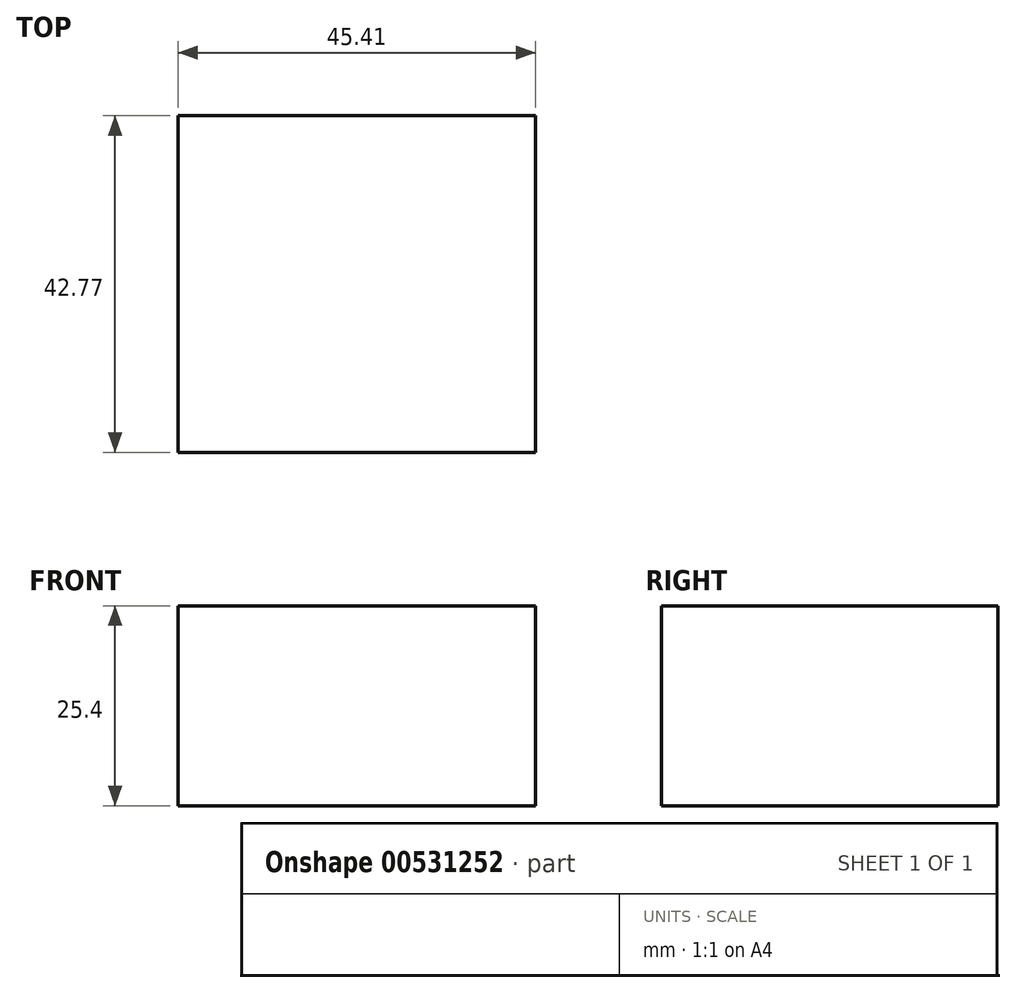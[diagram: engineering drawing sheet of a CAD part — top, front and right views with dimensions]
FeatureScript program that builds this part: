
annotation { "Feature Type Name" : "Feature", "Feature Type Description" : "" }
export const myFeature = defineFeature(function(context is Context, id is Id, definition is map)
    precondition{}
    {
        {
            var Q0;
            Q0=qCreatedBy(makeId("Top.planeOp"),FACE);
            var sketch = newSketch(context, id + "F0", { "sketchPlane" : qUnion([Q0])});
            skLineSegment(sketch, "E0.bottom", {"start": v(0, 0) * mm, "end": v(45.4, 0) * mm});
            skLineSegment(sketch, "E0.top", {"start": v(0, 42.77) * mm, "end": v(45.4, 42.77) * mm});
            skLineSegment(sketch, "E0.left", {"start": v(0, 0) * mm, "end": v(0, 42.77) * mm});
            skLineSegment(sketch, "E0.right", {"start": v(45.4, 0) * mm, "end": v(45.4, 42.77) * mm});
            skSolve(sketch);
        }
        {
            var Q0;
            Q0=makeQuery(id+"F0.imprint","IMPRINT",FACE,{"disambiguationData":[TD([[makeQuery(id+"F0.imprint","IMPRINT",EDGE,{"derivedFrom":sQuery(id+"F0.wireOp",EDGE,"E0.bottom")}),1.0]])]});
            extrude(context, id + "F1", {"entities" : qUnion([Q0]), "depth" : 25.4 * mm, "offsetDistance" : 25.4 * mm});
        }
    });
